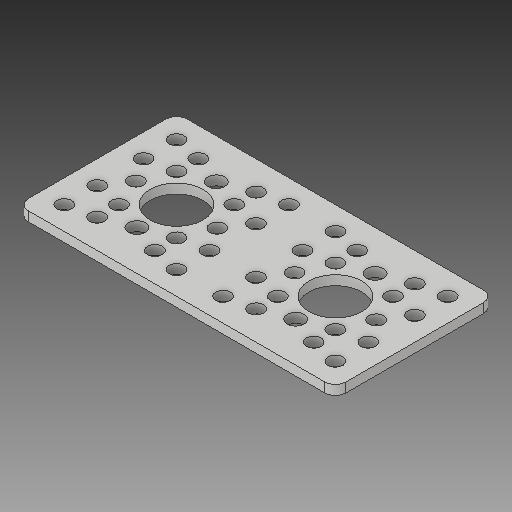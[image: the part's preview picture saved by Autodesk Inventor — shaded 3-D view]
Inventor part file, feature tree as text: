
AUTODESK INVENTOR PART (.ipt)
format: ipt  version: 2017 (Build 210142000, 142)  size: 222,208 bytes
history: native  units: in
note: dims shown in document units (in); Inventor stores cm internally (conversion verified against a paired STEP export)
features: fillet x1
ambient origin geometry x8: Origin, YZ Plane, XZ Plane, XY Plane, X Axis, Y Axis, Z Axis, Center Point
bodies: Solid1 (feature_tree)
feature tree (1):
  fillet  "Fillet1"  [1 undecoded]
note: 1 required parameter value undecoded (feature->parameter linkage not recoverable at this tier; creation-order binding heuristic only, values carry confidence <= 0.55)
